# Revit family: qqqq
name_source: partatom
category: Pipe Accessories
revit_build: Autodesk Revit 2018 (Build: 20170223_1515(x64)
units: mm (PartAtom-declared; Revit-internal decimal feet)

## family parameters
Always vertical = Yes
Cut with Voids When Loaded = No
OmniClass Number = 23.27.43.00
OmniClass Title = Pipe Fittings
Part Type = Valve - Breaks Into
Round Connector Dimension = Use Diameter
Shared = No
Work Plane-Based = No

## types (4) — shared parameters
Assembly Code = D2040100
BIMobject category = Joints
Description = Pneumatic axial valve
Design country = Italy
Edition number = 1
IFC Classification = Pipe Fitting
Keynote = 15410
Lookup Table Name = Pneumatic Axial Valve - 90740
Manufacturer = Aignep Spa
Manufacturer country = Italy
Manufacturer name = Aignep Spa
Material main = Aluminium
Model = 90740
OmniClass Code = 23-27 43 00
OmniClass Description = Pipe Fittings
Product Guid = a1df13ec-476c-4914-803c-121645f64a07
Product Material = AIGNEP - Brass - Yellow
Product SKU = Pneumatic-Axial-Valve-90740
Product certification = https://www.aignep.com
Product data url = https://www.bimobject.com
Product family = INFINITY
Product group = Valves
Product name = Pneumatic Axial Valve - 90740
Product url = https://www.aignep.com
QR code = https://www.bimobject.com
URL = https://www.aignep.com

## per-type parameters (varying)
| type | A | B | C | D1 | D2 | E | F | Nominal Diameter | Tick Size |
| D 32 | 198 mm | 46 mm | 89 mm | 6.2 mm | 7 mm  [stored 0.0229659 ft] | 52 mm | 92.6 mm | 32.000 mm | 25.6 mm |
| D 40 | 208 mm | 52 mm | 89 mm | 4.7 mm | 9.7 mm | 63 mm | 92.6 mm | 40.000 mm | 32 mm |
| D 50 | 249 mm | 63.5 mm | 109 mm | 6.5 mm | 14 mm  [stored 0.0459318 ft] | 73 mm | 110 mm | 50.000 mm | 40 mm |
| D 63 | 269 mm  [stored 0.882546 ft] | 57.5 mm | 139 mm | 5.77 mm | 21.2 mm | 94 mm  [stored 0.308399 ft] | 140.3 mm  [stored 0.460302 ft] | 63.000 mm | 50.4 mm |

note: [stored X ft] marks values corroborated as IEEE doubles in the binary element streams (Revit-internal decimal feet)

## geometry (parser evidence)
native form markers: Sweep x1
no freeform markers — native parametric forms only
